# Revit family: Space-ette_Water-Cooler_Legacy_Elkay-FD7003L1Z
name_source: partatom
category: Plumbing Fixtures
units: mm (PartAtom-declared; Revit-internal decimal feet)

## family parameters
Always vertical = Yes
Cut with Voids When Loaded = No
Maintain Annotation Orientation = No
OmniClass Number = 23.45.05.14.14
OmniClass Title = Sinks/Lavatories
Part Type = Normal
Room Calculation Point = No
Round Connector Dimension = Use Diameter
Shared = No
Work Plane-Based = No

## types (1)
- FD7003L1Z (Space-ette™ Cooler Legacy Floor Model Non-filtered Refrigerated)
    Approx. Shipping Weight (lbs) = 54
    Assembly Code = D2010800
    Bottom Plate Len = 11.200"
    Bottom Plate Width = 11.000"
    Btm plt walls dist. = 11.813"
    Btm plt walls length = 11.200"
    Chilling Capacity = 3.0 GPH
    Default Elevation = 0.000"
    Description = Space-ette™ Cooler Legacy Floor Model Non-filtered Refrigerated 3 GPH Light Gray Granite
    Dimensions (L x W x H) = 12 inch x 12 inch x 38 inch
    Frnt Pnl wall dist. = 10.960"
    Frnt panel Height = 33.403"
    Frnt pnl Len. = 10.850"
    Height = 38.000"
    Inlet Connection Size (inch) = 0.375"
    Installation Location = Indoor
    Length = 12.000"
    Main Material = Finish-Elkay-Stainless Steel
    Manufacturer = Elkay (by Zurn Elkay Water Solutions)
    Manufacturer Brand = Elkay Manufacturer Company
    Model = FD7003L1Z
    Mounting Type = Floor Mount/Freestanding
    Outlet Connection Size (inch) = 1.250"
    Panel Length = 11.900"
    Panel Width = 11.900"
    Product Documentation Link = https://www.elkayfiles.com
    Product Installation Sheet URL = https://www.elkayfiles.com
    Product Page URL = https://www.elkay.com
    Product Weight (lbs) = 51
    Product data URL = https://bimobject.com
    Repair Parts URL = https://www.elkayfiles.com
    URL = https://www.elkay.com
    Width = 12.000"
    Width base plane = 5.600"
    back Btm plt walls dist. = 5.907"

## geometry (parser evidence)
native form markers: Sweep x6
no freeform markers — native parametric forms only
